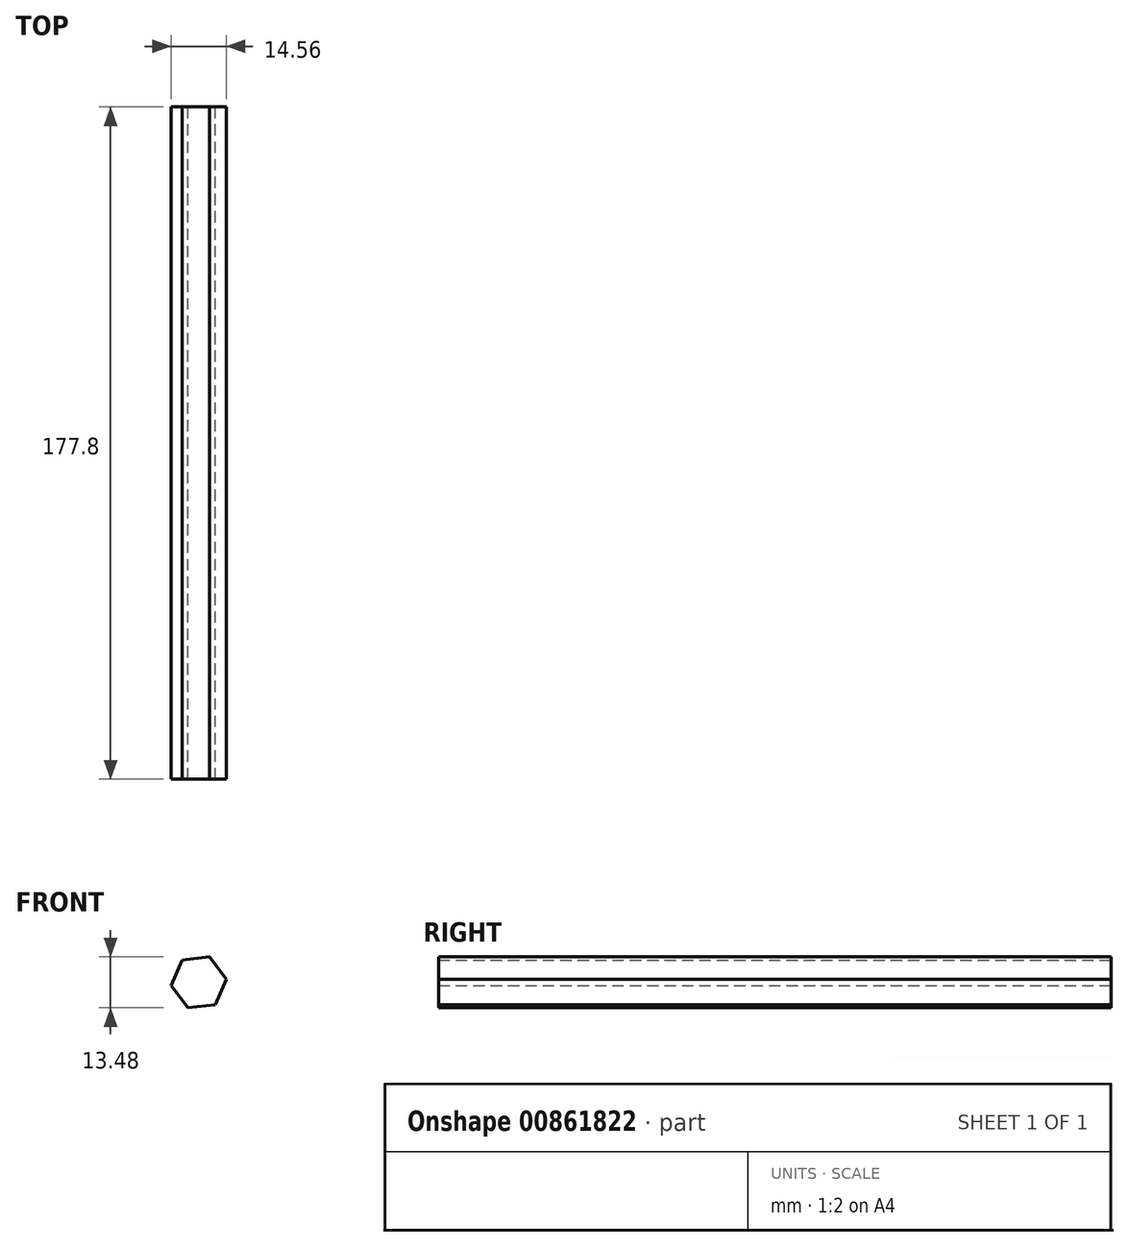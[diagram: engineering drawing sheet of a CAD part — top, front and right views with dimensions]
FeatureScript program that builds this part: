
annotation { "Feature Type Name" : "Feature", "Feature Type Description" : "" }
export const myFeature = defineFeature(function(context is Context, id is Id, definition is map)
    precondition{}
    {
        {
            var Q0;
            Q0=qCreatedBy(makeId("Front.planeOp"),FACE);
            var sketch = newSketch(context, id + "F0", { "sketchPlane" : qUnion([Q0])});
            skCircle(sketch, "E0.cCircle", {"center": v(0, 0) * mm, "radius": 6.35 * mm, "construction": true});
            skLineSegment(sketch, "E0.0", {"start": v(2.9, 6.74) * mm, "end": v(7.28, 0.86) * mm});
            skLineSegment(sketch, "E0.1", {"start": v(7.28, 0.86) * mm, "end": v(4.39, -5.87) * mm});
            skLineSegment(sketch, "E0.2", {"start": v(4.39, -5.87) * mm, "end": v(-2.9, -6.74) * mm});
            skLineSegment(sketch, "E0.3", {"start": v(-2.9, -6.74) * mm, "end": v(-7.28, -0.86) * mm});
            skLineSegment(sketch, "E0.4", {"start": v(-7.28, -0.86) * mm, "end": v(-4.39, 5.87) * mm});
            skLineSegment(sketch, "E0.5", {"start": v(-4.39, 5.87) * mm, "end": v(2.9, 6.74) * mm});
            skPoint(sketch, "E0.0.midPoint", {"position": v(5.09, 3.8) * mm});
            skSolve(sketch);
        }
        {
            var Q0;
            Q0=makeQuery(id+"F0.imprint","IMPRINT",FACE,{"disambiguationData":[TD([[makeQuery(id+"F0.imprint","IMPRINT",EDGE,{"derivedFrom":sQuery(id+"F0.wireOp",EDGE,"E0.0")}),-1.0]])]});
            extrude(context, id + "F1", {"entities" : qUnion([Q0]), "depth" : 177.8 * mm, "offsetDistance" : 25.4 * mm});
        }
    });
